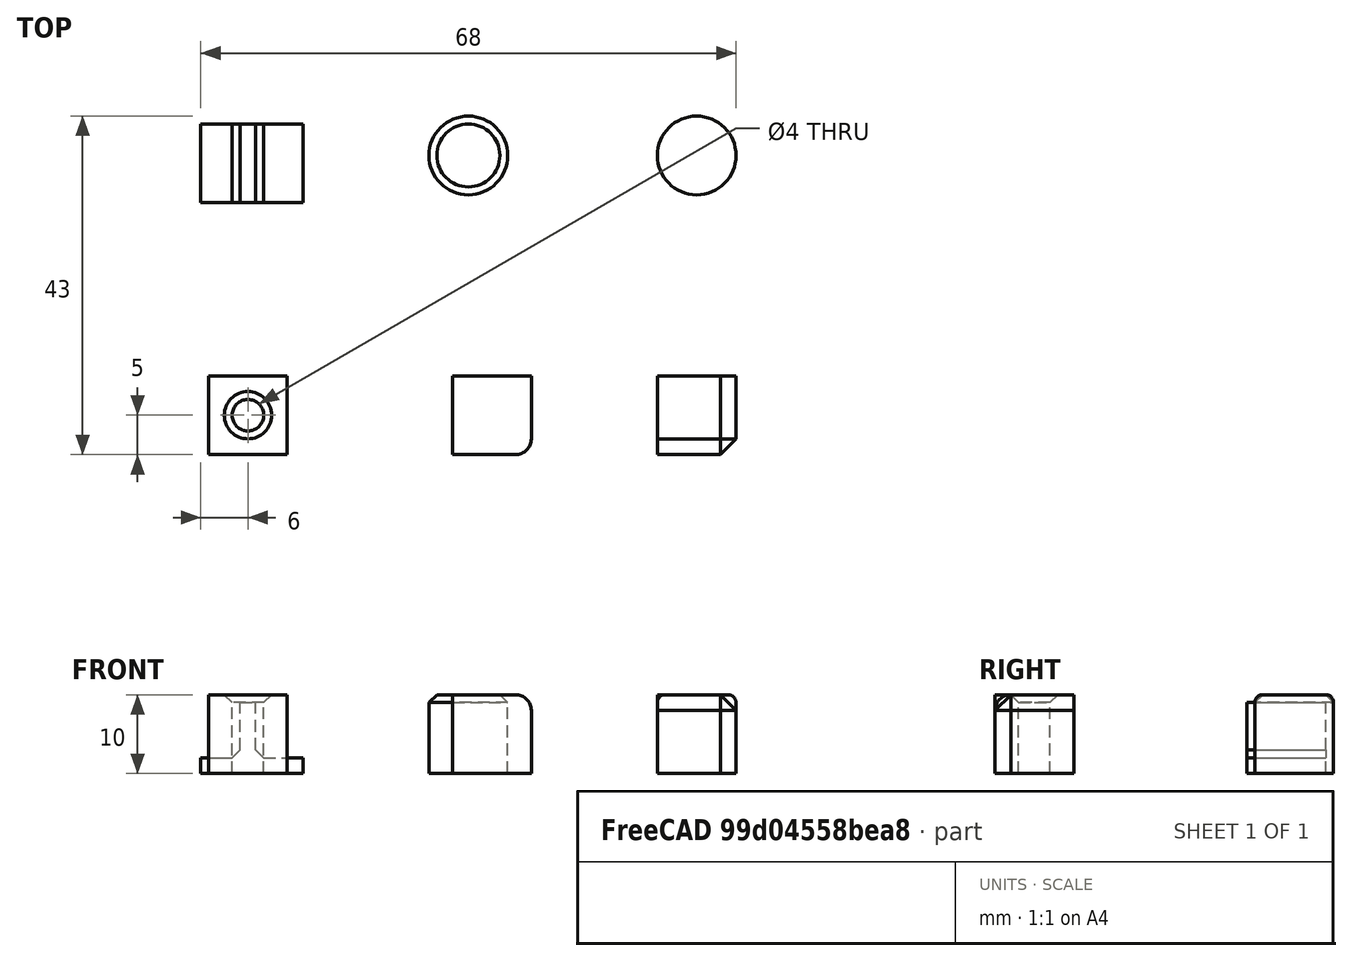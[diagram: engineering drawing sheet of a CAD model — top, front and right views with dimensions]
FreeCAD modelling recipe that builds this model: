
FCSTD DOCUMENT  (FreeCAD 1.0R39319 (Git))
Label: ojt1_t12p01_roundings_chamfers_reinforcements
License: All rights reserved
LicenseURL: https://en.wikipedia.org/wiki/All_rights_reserved
objects: Part::Box×5, Part::Chamfer×5, Part::FeaturePython×3, Part::Fillet×2, Part::Cut×1, Part::MultiFuse×1
note: 17 computed .brp shape members not serialized (recipe doc carries the construction recipe); baked Part::Feature solids carry a one-line shape summary decoded from their .brp

FEATURE [Part::Box] Box  label="Cub"
  AttacherType = Attacher::AttachEngine3D
  Height = 10
  Length = 10
  Placement = pos=(31,0,0) rot=(0,0,1;0rad)
  Width = 10
FEATURE [Part::Box] Box001  label="Cub001"
  AttacherType = Attacher::AttachEngine3D
  Height = 10
  Length = 10
  Placement = pos=(57,0,0) rot=(0,0,1;0rad)
  Width = 10
FEATURE [Part::Box] Box002  label="Cub002"
  AttacherType = Attacher::AttachEngine3D
  Height = 10
  Length = 10
  Width = 10
FEATURE [Part::FeaturePython] Tube  # WARN: FeaturePython — macro-defined, semantics opaque (R4)
  AttacherType = Attacher::AttachEngine3D
  Height = 10
  InnerRadius = 0
  OuterRadius = 2
  Placement = pos=(5,5,0) rot=(0,0,1;0rad)
FEATURE [Part::Cut] Cut
  Base = -> Box002
  Refine = true
  Tool = -> Tube
FEATURE [Part::FeaturePython] Tube001  # WARN: FeaturePython — macro-defined, semantics opaque (R4)
  AttacherType = Attacher::AttachEngine3D
  Height = 10
  InnerRadius = 0
  OuterRadius = 5
  Placement = pos=(62,38,0) rot=(0,0,1;0rad)
FEATURE [Part::FeaturePython] Tube002  # WARN: FeaturePython — macro-defined, semantics opaque (R4)
  AttacherType = Attacher::AttachEngine3D
  Height = 10
  InnerRadius = 0
  OuterRadius = 5
  Placement = pos=(33,38,0) rot=(0,0,1;0rad)
FEATURE [Part::Box] Box003  label="Cub003"
  AttacherType = Attacher::AttachEngine3D
  Height = 2
  Length = 13
  Placement = pos=(-1,32,0) rot=(0,0,1;0rad)
  Width = 10
FEATURE [Part::Box] Box004  label="Cub004"
  AttacherType = Attacher::AttachEngine3D
  Height = 9
  Length = 2
  Placement = pos=(4,32,0) rot=(0,0,1;0rad)
  Width = 10
FEATURE [Part::MultiFuse] Fusion
  Refine = true
  Shapes = -> [Box003,Box004]
FEATURE [Part::Fillet] Fillet
  Base = -> Box
  EdgeLinks = -> Box [Edge5,Edge6,Edge10]
  Edges = 3 edges r=2: [Edge5,Edge6,Edge10]
FEATURE [Part::Chamfer] Chamfer
  Base = -> Box001
  EdgeLinks = -> Box001 [Edge5,Edge6,Edge10]
  Edges = 3 edges r=2: [Edge5,Edge6,Edge10]
FEATURE [Part::Chamfer] Chamfer001
  Base = -> Cut
  EdgeLinks = -> Cut [Edge10]
  Edges = 1 edges r=1: [Edge10]
FEATURE [Part::Fillet] Fillet001
  Base = -> Tube001
  EdgeLinks = -> Tube001 [Edge1]
  Edges = 1 edges r=1: [Edge1]
FEATURE [Part::Chamfer] Chamfer002
  Base = -> Tube002
  EdgeLinks = -> Tube002 [Edge1]
  Edges = 1 edges r=1: [Edge1]
FEATURE [Part::Chamfer] Chamfer003
  Base = -> Fusion
  EdgeLinks = -> Fusion [Edge16]
  Edges = 1 edges r=1: [Edge16]
FEATURE [Part::Chamfer] Chamfer004
  Base = -> Chamfer003
  EdgeLinks = -> Chamfer003 [Edge27]
  Edges = 1 edges r=1: [Edge27]
